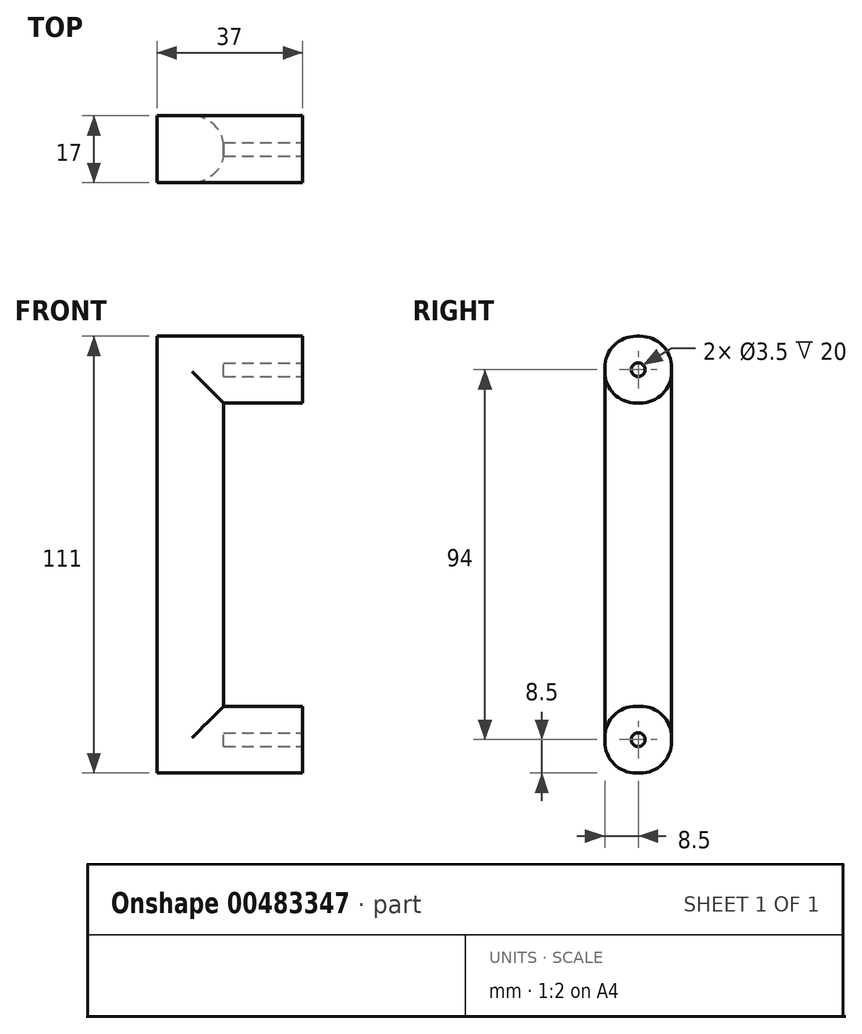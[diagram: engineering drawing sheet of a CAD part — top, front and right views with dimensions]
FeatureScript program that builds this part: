
annotation { "Feature Type Name" : "Feature", "Feature Type Description" : "" }
export const myFeature = defineFeature(function(context is Context, id is Id, definition is map)
    precondition{}
    {
        {
            var Q0;
            Q0=qCreatedBy(makeId("Front.planeOp"),FACE);
            var sketch = newSketch(context, id + "F0", { "sketchPlane" : qUnion([Q0])});
            skLineSegment(sketch, "E0.bottom", {"start": v(0, 0) * mm, "end": v(-20, 0) * mm});
            skLineSegment(sketch, "E0.top", {"start": v(0, 17) * mm, "end": v(-20, 17) * mm});
            skLineSegment(sketch, "E0.left", {"start": v(0, 0) * mm, "end": v(0, 17) * mm});
            skLineSegment(sketch, "E0.right", {"start": v(-20, 0) * mm, "end": v(-20, 17) * mm});
            skLineSegment(sketch, "E1.bottom", {"start": v(-20, 0) * mm, "end": v(-37, 0) * mm});
            skLineSegment(sketch, "E1.top", {"start": v(-20, 111) * mm, "end": v(-37, 111) * mm});
            skLineSegment(sketch, "E1.left", {"start": v(-20, 0) * mm, "end": v(-20, 111) * mm});
            skLineSegment(sketch, "E1.right", {"start": v(-37, 0) * mm, "end": v(-37, 111) * mm});
            skLineSegment(sketch, "E2.bottom", {"start": v(-20, 111) * mm, "end": v(0, 111) * mm});
            skLineSegment(sketch, "E2.top", {"start": v(-20, 94) * mm, "end": v(0, 94) * mm});
            skLineSegment(sketch, "E2.left", {"start": v(-20, 111) * mm, "end": v(-20, 94) * mm});
            skLineSegment(sketch, "E2.right", {"start": v(0, 111) * mm, "end": v(0, 94) * mm});
            skLineSegment(sketch, "E3", {"start": v(-20, 94) * mm, "end": v(-37, 94) * mm});
            skLineSegment(sketch, "E4", {"start": v(-20, 17) * mm, "end": v(-37, 17) * mm});
            skLineSegment(sketch, "E5", {"start": v(-20, 17) * mm, "end": v(-37, 0) * mm});
            skLineSegment(sketch, "E6", {"start": v(-37, 17) * mm, "end": v(-28.5, 8.5) * mm});
            skLineSegment(sketch, "E7", {"start": v(-20, 111) * mm, "end": v(-37, 94) * mm});
            skLineSegment(sketch, "E8", {"start": v(-37, 111) * mm, "end": v(-28.5, 102.5) * mm});
            skSolve(sketch);
        }
        {
            var Q0;
            Q0 = qSketchRegion(id + "F0", true);
            extrude(context, id + "F1", {"entities" : qUnion([Q0]), "endBound" : BoundingType.SYMMETRIC, "depth" : 17 * mm});
        }
        {
            var Q0;
            Q0=makeQuery(id+"F1.opExtrude","SWEPT_FACE",FACE,{"disambiguationData":[OSD([sQuery(id+"F0.wireOp",EDGE,"E0.left")])]});
            var sketch = newSketch(context, id + "F2", { "sketchPlane" : qUnion([Q0])});
            skLineSegment(sketch, "E9", {"start": v(-8.5, 0) * mm, "end": v(8.5, 17) * mm});
            skLineSegment(sketch, "E10", {"start": v(0, 8.5) * mm, "end": v(8.5, 0) * mm});
            skCircle(sketch, "E11", {"center": v(0, 8.5) * mm, "radius": 1.75 * mm});
            skLineSegment(sketch, "E12", {"start": v(-8.5, 111) * mm, "end": v(8.5, 94) * mm});
            skLineSegment(sketch, "E13", {"start": v(-8.5, 94) * mm, "end": v(0, 102.5) * mm});
            skCircle(sketch, "E14", {"center": v(0, 102.5) * mm, "radius": 1.75 * mm});
            skSolve(sketch);
        }
        {
            var Q0;
            {var subQ0=sQuery(id+"F2.wireOp",EDGE,"E12");var subQ1=makeQuery(id+"F2.imprint","INTERSECT",VERTEX,{"derivedFrom":[subQ0,sQuery(id+"F2.wireOp",EDGE,"E13")]});Q0=makeQuery(id+"F2.imprint","IMPRINT",FACE,{"disambiguationData":[TD([[makeQuery(id+"F2.imprint","IMPRINT",EDGE,{"disambiguationData":[TD([[subQ1,1.0]])],"derivedFrom":subQ0}),1.0]])]});}
            var Q1;
            {var subQ0=sQuery(id+"F2.wireOp",EDGE,"E13");var subQ1=sQuery(id+"F2.wireOp",EDGE,"E12");var subQ2=makeQuery(id+"F2.imprint","INTERSECT",VERTEX,{"derivedFrom":[subQ1,subQ0]});Q1=makeQuery(id+"F2.imprint","IMPRINT",FACE,{"disambiguationData":[TD([[makeQuery(id+"F2.imprint","IMPRINT",EDGE,{"disambiguationData":[TD([[subQ2,-1.0]])],"derivedFrom":subQ1}),-1.0]])]});}
            var Q2;
            {var subQ0=sQuery(id+"F2.wireOp",EDGE,"E13");var subQ1=sQuery(id+"F2.wireOp",EDGE,"E12");var subQ2=makeQuery(id+"F2.imprint","INTERSECT",VERTEX,{"derivedFrom":[subQ1,subQ0]});Q2=makeQuery(id+"F2.imprint","IMPRINT",FACE,{"disambiguationData":[TD([[makeQuery(id+"F2.imprint","IMPRINT",EDGE,{"disambiguationData":[TD([[subQ2,1.0]])],"derivedFrom":subQ1}),-1.0]])]});}
            var Q3;
            Q3=sQuery(id+"F2.wireOp",EDGE,"E14");
            extrude(context, id + "F3", {"entities" : qUnion([Q0, Q1, Q2]), "operationType" : NewBodyOperationType.REMOVE, "surfaceEntities" : qUnion([Q3]), "oppositeDirection" : true, "depth" : 20 * mm});
        }
        {
            var Q0;
            {var subQ0=sQuery(id+"F2.wireOp",EDGE,"E10");var subQ1=sQuery(id+"F2.wireOp",EDGE,"E9");var subQ2=makeQuery(id+"F2.imprint","INTERSECT",VERTEX,{"derivedFrom":[subQ1,subQ0]});Q0=makeQuery(id+"F2.imprint","IMPRINT",FACE,{"disambiguationData":[TD([[makeQuery(id+"F2.imprint","IMPRINT",EDGE,{"disambiguationData":[TD([[subQ2,1.0]])],"derivedFrom":subQ1}),-1.0]])]});}
            var Q1;
            {var subQ0=sQuery(id+"F2.wireOp",EDGE,"E10");var subQ1=sQuery(id+"F2.wireOp",EDGE,"E9");var subQ2=makeQuery(id+"F2.imprint","INTERSECT",VERTEX,{"derivedFrom":[subQ1,subQ0]});Q1=makeQuery(id+"F2.imprint","IMPRINT",FACE,{"disambiguationData":[TD([[makeQuery(id+"F2.imprint","IMPRINT",EDGE,{"disambiguationData":[TD([[subQ2,-1.0]])],"derivedFrom":subQ1}),-1.0]])]});}
            var Q2;
            {var subQ0=sQuery(id+"F2.wireOp",EDGE,"E9");var subQ1=makeQuery(id+"F2.imprint","INTERSECT",VERTEX,{"derivedFrom":[subQ0,sQuery(id+"F2.wireOp",EDGE,"E10")]});Q2=makeQuery(id+"F2.imprint","IMPRINT",FACE,{"disambiguationData":[TD([[makeQuery(id+"F2.imprint","IMPRINT",EDGE,{"disambiguationData":[TD([[subQ1,1.0]])],"derivedFrom":subQ0}),1.0]])]});}
            var Q3;
            Q3=sQuery(id+"F2.wireOp",EDGE,"E11");
            extrude(context, id + "F4", {"entities" : qUnion([Q0, Q1, Q2]), "operationType" : NewBodyOperationType.REMOVE, "surfaceEntities" : qUnion([Q3]), "oppositeDirection" : true, "depth" : 20 * mm});
        }
        {
            var Q0;
            Q0=makeQuery(id+"F1.opExtrude","CAP_EDGE",EDGE,{"disambiguationData":[OSD([sQuery(id+"F0.wireOp",EDGE,"E1.left")])],"isStart":true});
            var Q1;
            Q1=makeQuery(id+"F1.opExtrude","CAP_EDGE",EDGE,{"disambiguationData":[OSD([sQuery(id+"F0.wireOp",EDGE,"E1.left")])],"isStart":false});
            var Q2;
            Q2=makeQuery(id+"F1.opExtrude","CAP_EDGE",EDGE,{"disambiguationData":[OSD([sQuery(id+"F0.wireOp",EDGE,"E2.top")])],"isStart":true});
            var Q3;
            Q3=makeQuery(id+"F1.opExtrude","CAP_EDGE",EDGE,{"disambiguationData":[OSD([sQuery(id+"F0.wireOp",EDGE,"E2.top")])],"isStart":false});
            var Q4;
            Q4=makeQuery(id+"F1.opExtrude","CAP_EDGE",EDGE,{"disambiguationData":[OSD([sQuery(id+"F0.wireOp",EDGE,"E0.top")])],"isStart":false});
            var Q5;
            Q5=makeQuery(id+"F1.opExtrude","CAP_EDGE",EDGE,{"disambiguationData":[OSD([sQuery(id+"F0.wireOp",EDGE,"E0.top")])],"isStart":true});
            var Q6;
            Q6=makeQuery(id+"F1.opExtrude","CAP_EDGE",EDGE,{"disambiguationData":[OSD([sQuery(id+"F0.wireOp",EDGE,"E0.bottom"),sQuery(id+"F0.wireOp",EDGE,"E1.bottom")])],"isStart":false});
            var Q7;
            Q7=makeQuery(id+"F1.opExtrude","CAP_EDGE",EDGE,{"disambiguationData":[OSD([sQuery(id+"F0.wireOp",EDGE,"E0.bottom"),sQuery(id+"F0.wireOp",EDGE,"E1.bottom")])],"isStart":true});
            var Q8;
            Q8=makeQuery(id+"F1.opExtrude","CAP_EDGE",EDGE,{"disambiguationData":[OSD([sQuery(id+"F0.wireOp",EDGE,"E1.top"),sQuery(id+"F0.wireOp",EDGE,"E2.bottom")])],"isStart":false});
            var Q9;
            Q9=makeQuery(id+"F1.opExtrude","CAP_EDGE",EDGE,{"disambiguationData":[OSD([sQuery(id+"F0.wireOp",EDGE,"E1.top"),sQuery(id+"F0.wireOp",EDGE,"E2.bottom")])],"isStart":true});
            fillet(context, id + "F5", {"entities" : qUnion([Q0, Q1, Q2, Q3, Q4, Q5, Q6, Q7, Q8, Q9]), "radius" : 8 * mm, "tangentPropagation" : true, "allowEdgeOverflow" : false});
        }
    });
